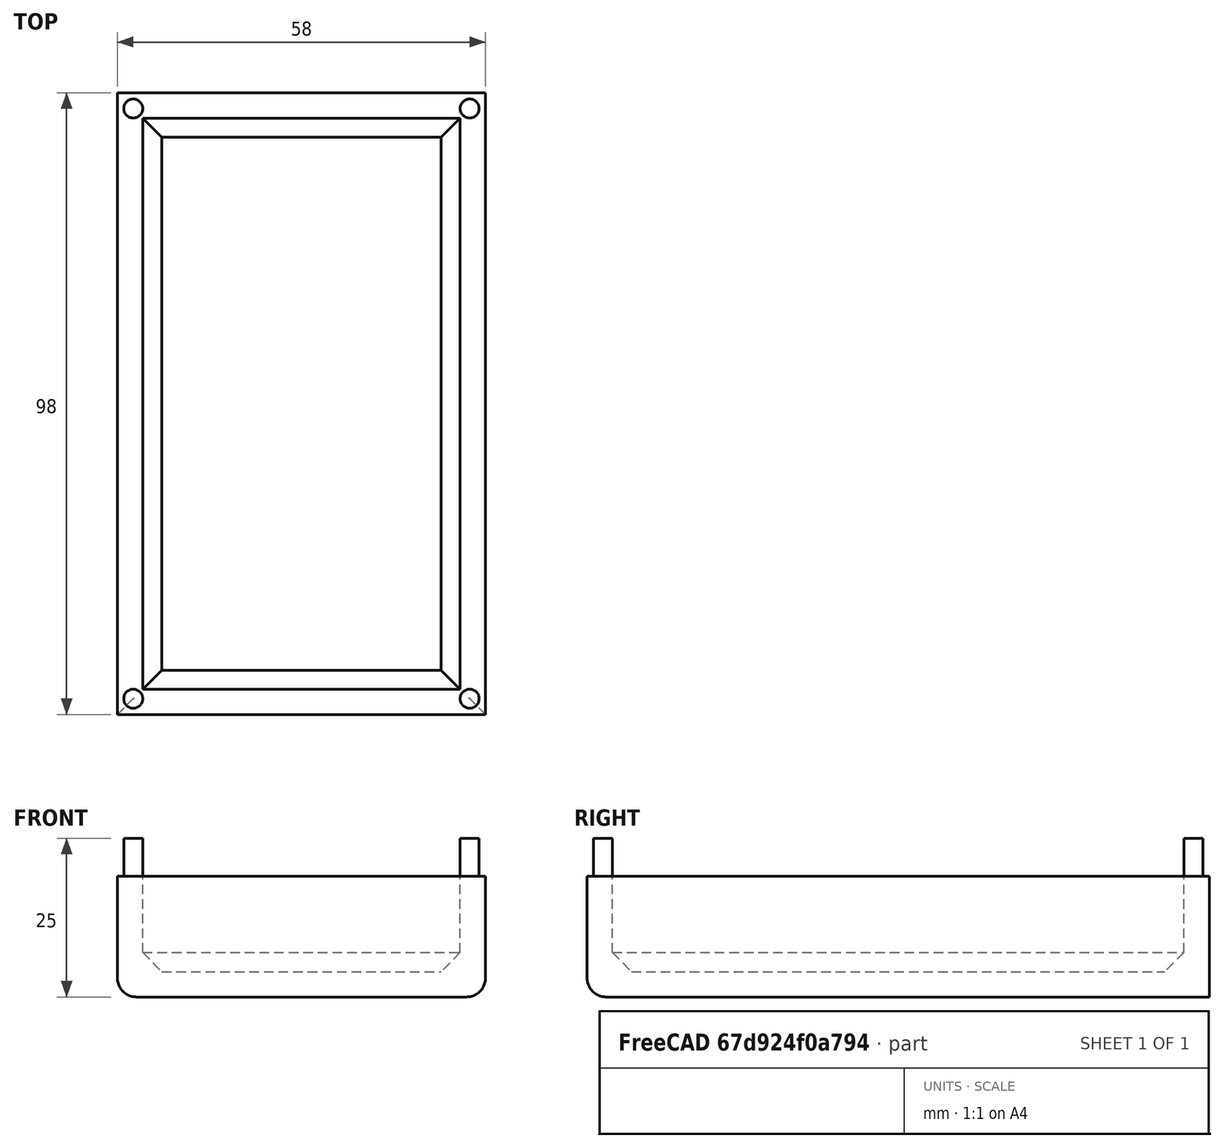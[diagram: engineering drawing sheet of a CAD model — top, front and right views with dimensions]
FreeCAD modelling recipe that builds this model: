
FCSTD DOCUMENT  (FreeCAD 0.17R13541 (Git))
Label: LifelineCase_Bottom
License: All rights reserved
LicenseURL: http://en.wikipedia.org/wiki/All_rights_reserved
objects: Part::Cylinder×4, Part::Box×2, Part::Chamfer×1, Part::Cut×1, Part::Fillet×1, Part::MultiFuse×1
note: 10 computed .brp shape members not serialized (recipe doc carries the construction recipe); baked Part::Feature solids carry a one-line shape summary decoded from their .brp

FEATURE [Part::Box] Box  label="Case"
  AttacherType = Attacher::AttachEngine3D
  Height = 19
  Length = 58
  Width = 98
FEATURE [Part::Box] Box001  label="Cutout"
  AttacherType = Attacher::AttachEngine3D
  Height = 15
  Length = 50
  Placement = pos=(4,4,4) rot=(0,0,1;0rad)
  Width = 90
FEATURE [Part::Cylinder] Cylinder
  Angle = 360
  AttacherType = Attacher::AttachEngine3D
  Height = 6
  Placement = pos=(2.5,2.5,19) rot=(0,0,1;0rad)
  Radius = 1.5
FEATURE [Part::Cylinder] Cylinder001
  Angle = 360
  AttacherType = Attacher::AttachEngine3D
  Height = 6
  Placement = pos=(55.5,2.5,19) rot=(0,0,1;0rad)
  Radius = 1.5
FEATURE [Part::Cylinder] Cylinder002
  Angle = 360
  AttacherType = Attacher::AttachEngine3D
  Height = 6
  Placement = pos=(2.5,95.5,19) rot=(0,0,1;0rad)
  Radius = 1.5
FEATURE [Part::Cylinder] Cylinder003
  Angle = 360
  AttacherType = Attacher::AttachEngine3D
  Height = 6
  Placement = pos=(55.5,95.5,19) rot=(0,0,1;0rad)
  Radius = 1.5
FEATURE [Part::Chamfer] Chamfer
  Base = -> Box001
  Edges = 4 edges r=3: [Edge4,Edge8,Edge9,Edge11]
FEATURE [Part::Cut] Cut
  Base = -> Box
  Tool = -> Chamfer
FEATURE [Part::Fillet] Fillet
  Base = -> Cut
  Edges = 3 edges r=3: [Edge4,Edge5,Edge16]
FEATURE [Part::MultiFuse] Fusion
  Shapes = -> [Fillet,Cylinder001,Cylinder002,Cylinder,Cylinder003]
